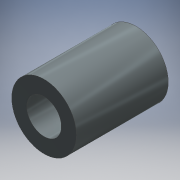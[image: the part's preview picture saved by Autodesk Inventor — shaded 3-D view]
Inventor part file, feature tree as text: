
AUTODESK INVENTOR PART (.ipt)
format: ipt  version: 2016 (Build 200138000, 138)  size: 107,008 bytes
history: native  units: mm
features: extrude x1, sketch x1
ambient origin geometry x8: Origin, YZ Plane, XZ Plane, XY Plane, X Axis, Y Axis, Z Axis, Center Point
bodies: Solid1 (feature_tree)
feature tree (2):
  extrude  "Extrusion1"  Depth=16.7mm
  sketch  "Sketch1"  dims[d0=6.3mm d1=11.75mm d2=16.7mm d3=0.0mm]
